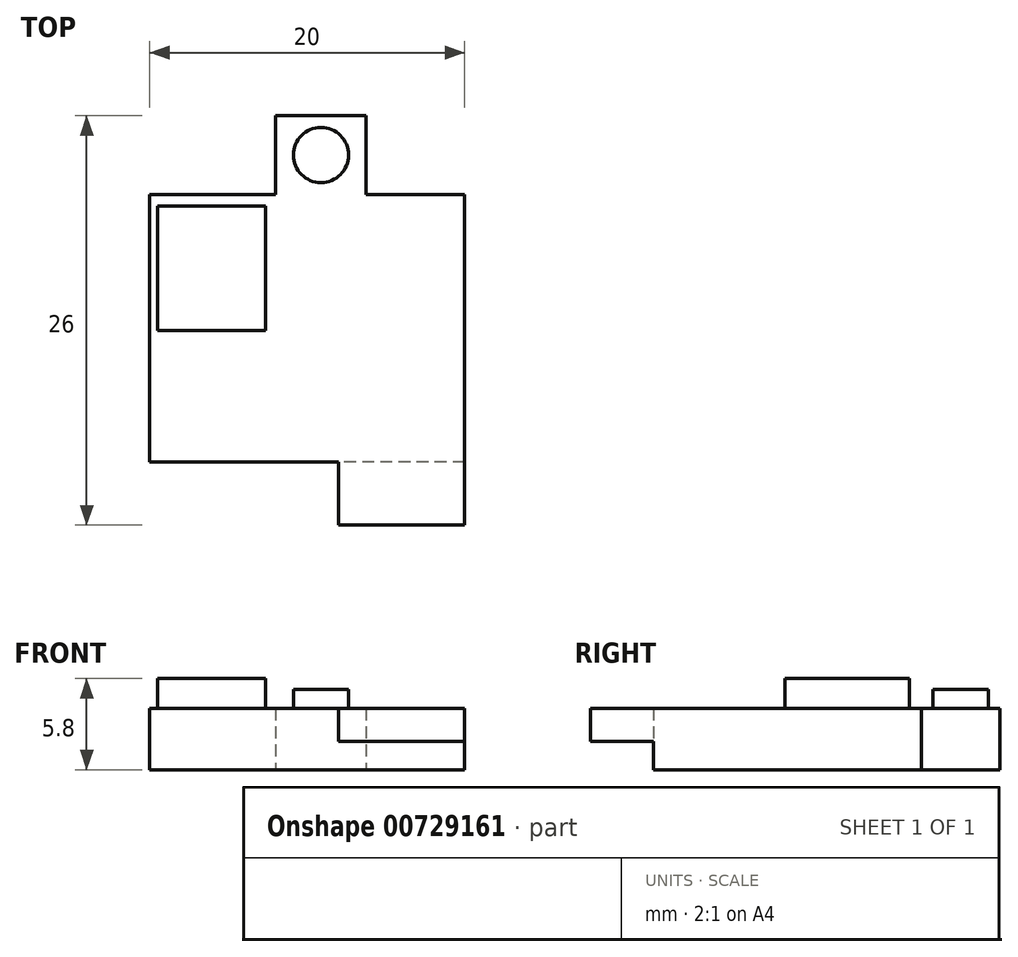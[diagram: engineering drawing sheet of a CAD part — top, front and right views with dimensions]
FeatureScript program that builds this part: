
annotation { "Feature Type Name" : "Feature", "Feature Type Description" : "" }
export const myFeature = defineFeature(function(context is Context, id is Id, definition is map)
    precondition{}
    {
        {
            var Q0;
            Q0=qCreatedBy(makeId("Top.planeOp"),FACE);
            var sketch = newSketch(context, id + "F0", { "sketchPlane" : qUnion([Q0])});
            skLineSegment(sketch, "E0.bottom", {"start": v(10, 8.5) * mm, "end": v(3.75, 8.5) * mm});
            skLineSegment(sketch, "E0.top", {"start": v(10, -8.5) * mm, "end": v(-10, -8.5) * mm});
            skLineSegment(sketch, "E0.left", {"start": v(10, 8.5) * mm, "end": v(10, -8.5) * mm});
            skLineSegment(sketch, "E0.right", {"start": v(-10, 8.5) * mm, "end": v(-10, -8.5) * mm});
            skPoint(sketch, "E0.middle", {"position": v(0, 0) * mm});
            skLineSegment(sketch, "E1.top", {"start": v(-2, 13.5) * mm, "end": v(3.75, 13.5) * mm});
            skLineSegment(sketch, "E1.left", {"start": v(-2, 8.5) * mm, "end": v(-2, 13.5) * mm});
            skLineSegment(sketch, "E1.right", {"start": v(3.75, 8.5) * mm, "end": v(3.75, 13.5) * mm});
            skLineSegment(sketch, "E2.trimOffspring", {"start": v(-2, 8.5) * mm, "end": v(-10, 8.5) * mm});
            skSolve(sketch);
        }
        {
            var Q0;
            Q0=makeQuery(id+"F0.imprint","IMPRINT",FACE,{"disambiguationData":[TD([[makeQuery(id+"F0.imprint","IMPRINT",EDGE,{"derivedFrom":sQuery(id+"F0.wireOp",EDGE,"E0.bottom")}),1.0]])]});
            extrude(context, id + "F1", {"entities" : qUnion([Q0]), "depth" : 2.1 * mm, "offsetDistance" : 25 * mm, "hasSecondDirection" : true, "secondDirectionOppositeDirection" : true, "secondDirectionDepth" : 1.8 * mm});
        }
        {
            var Q0;
            Q0=qCreatedBy(makeId("Top.planeOp"),FACE);
            var sketch = newSketch(context, id + "F2", { "sketchPlane" : qUnion([Q0])});
            skPoint(sketch, "E3.0", {"position": v(-2, 8.5) * mm});
            skPoint(sketch, "E4.0", {"position": v(3.75, 13.5) * mm});
            skLineSegment(sketch, "E5", {"start": v(-2, 8.5) * mm, "end": v(3.75, 13.5) * mm, "construction": true});
            skCircle(sketch, "E6", {"center": v(0.88, 11) * mm, "radius": 1.75 * mm});
            skSolve(sketch);
        }
        {
            var Q0;
            Q0 = qSketchRegion(id + "F2", true);
            extrude(context, id + "F3", {"entities" : qUnion([Q0]), "operationType" : NewBodyOperationType.ADD, "depth" : 3.3 * mm, "offsetDistance" : 25 * mm});
        }
        {
            var Q0;
            Q0=qCreatedBy(makeId("Top.planeOp"),FACE);
            var sketch = newSketch(context, id + "F4", { "sketchPlane" : qUnion([Q0])});
            skLineSegment(sketch, "E7.0", {"start": v(-10, 8.5) * mm, "end": v(-10, -8.5) * mm, "construction": true});
            skLineSegment(sketch, "E8.0", {"start": v(-2, 8.5) * mm, "end": v(-10, 8.5) * mm, "construction": true});
            skLineSegment(sketch, "E9.bottom", {"start": v(-9.5, 7.75) * mm, "end": v(-2.65, 7.75) * mm});
            skLineSegment(sketch, "E9.top", {"start": v(-9.5, -0.15) * mm, "end": v(-2.65, -0.15) * mm});
            skLineSegment(sketch, "E9.left", {"start": v(-9.5, 7.75) * mm, "end": v(-9.5, -0.15) * mm});
            skLineSegment(sketch, "E9.right", {"start": v(-2.65, 7.75) * mm, "end": v(-2.65, -0.15) * mm});
            skSolve(sketch);
        }
        {
            var Q0;
            Q0 = qSketchRegion(id + "F4", true);
            extrude(context, id + "F5", {"entities" : qUnion([Q0]), "operationType" : NewBodyOperationType.ADD, "depth" : 4 * mm, "offsetDistance" : 25 * mm});
        }
        {
            var Q0;
            Q0=makeQuery(id+"F1.opExtrude","SWEPT_FACE",FACE,{"disambiguationData":[OSD([sQuery(id+"F0.wireOp",EDGE,"E0.top")])]});
            var sketch = newSketch(context, id + "F6", { "sketchPlane" : qUnion([Q0])});
            skLineSegment(sketch, "E10.bottom", {"start": v(10, 2.1) * mm, "end": v(2, 2.1) * mm});
            skLineSegment(sketch, "E10.top", {"start": v(10, 0) * mm, "end": v(2, 0) * mm});
            skLineSegment(sketch, "E10.left", {"start": v(10, 2.1) * mm, "end": v(10, 0) * mm});
            skLineSegment(sketch, "E10.right", {"start": v(2, 2.1) * mm, "end": v(2, 0) * mm});
            skSolve(sketch);
        }
        {
            var Q0;
            Q0 = qSketchRegion(id + "F6", true);
            extrude(context, id + "F7", {"entities" : qUnion([Q0]), "operationType" : NewBodyOperationType.ADD, "depth" : 4 * mm, "offsetDistance" : 25 * mm});
        }
    });
